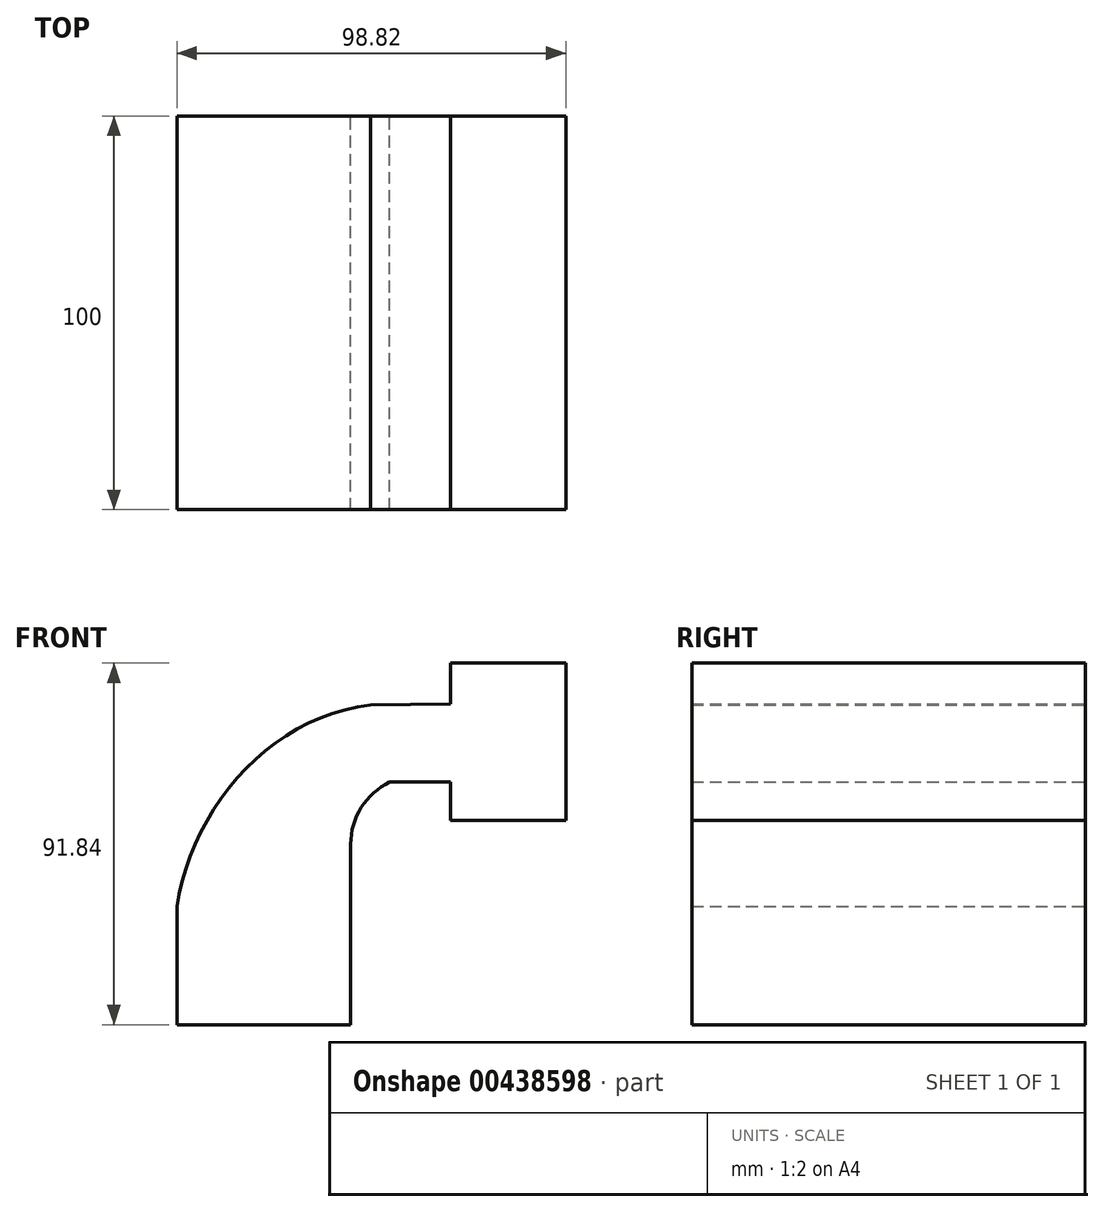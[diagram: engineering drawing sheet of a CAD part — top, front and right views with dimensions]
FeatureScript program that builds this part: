
annotation { "Feature Type Name" : "Feature", "Feature Type Description" : "" }
export const myFeature = defineFeature(function(context is Context, id is Id, definition is map)
    precondition{}
    {
        {
            var Q0;
            Q0=qCreatedBy(makeId("Front.planeOp"),FACE);
            var sketch = newSketch(context, id + "F0", { "sketchPlane" : qUnion([Q0])});
            skLineSegment(sketch, "E0.bottom", {"start": v(22.09, -15) * mm, "end": v(-22.09, -15) * mm});
            skLineSegment(sketch, "E0.top", {"start": v(22.09, 15) * mm, "end": v(-22.09, 15) * mm});
            skLineSegment(sketch, "E0.left", {"start": v(22.09, -15) * mm, "end": v(22.09, 15) * mm});
            skLineSegment(sketch, "E0.right", {"start": v(-22.09, -15) * mm, "end": v(-22.09, 15) * mm});
            skPoint(sketch, "E0.middle", {"position": v(0, 0) * mm});
            skLineSegment(sketch, "E1", {"start": v(22.09, 15) * mm, "end": v(22.09, 30.87) * mm});
            skArc(sketch, "E2", {"start": v(22.09, 30.87) * mm, "mid": v(24.77, 40.18) * mm, "end": v(32, 46.62) * mm});
            skLineSegment(sketch, "E3.bottom", {"start": v(76.73, 36.84) * mm, "end": v(47.44, 36.84) * mm});
            skLineSegment(sketch, "E3.top", {"start": v(76.73, 76.84) * mm, "end": v(47.44, 76.84) * mm});
            skLineSegment(sketch, "E3.left", {"start": v(76.73, 36.84) * mm, "end": v(76.73, 76.84) * mm});
            skLineSegment(sketch, "E3.right", {"start": v(47.44, 36.84) * mm, "end": v(47.44, 76.84) * mm});
            skPoint(sketch, "E3.middle", {"position": v(62.09, 56.84) * mm});
            skLineSegment(sketch, "E4.0", {"start": v(27.18, 66.24) * mm, "end": v(62.09, 66.62) * mm});
            skArc(sketch, "E4.1", {"start": v(2.09, 30.87) * mm, "mid": v(9, 52.55) * mm, "end": v(27.18, 66.24) * mm});
            skLineSegment(sketch, "E4.2", {"start": v(2.09, 15) * mm, "end": v(2.09, 30.87) * mm});
            skLineSegment(sketch, "E5", {"start": v(62.09, 56.84) * mm, "end": v(62.09, 76.84) * mm});
            skLineSegment(sketch, "E6", {"start": v(62.09, 76.84) * mm, "end": v(62.09, 56.84) * mm});
            skLineSegment(sketch, "E7", {"start": v(62.09, 56.84) * mm, "end": v(62.09, 36.84) * mm});
            skLineSegment(sketch, "E8", {"start": v(32, 46.62) * mm, "end": v(62.09, 46.62) * mm});
            skFitSpline(sketch, "E9", {"points": [v(-22.09, 15) * mm, v(27.18, 66.24) * mm], "startDerivative": vector(11.48, 74.86) * mm, "endDerivative": vector(77.05, 8.88) * mm});
            skSolve(sketch);
        }
        {
            var Q0;
            Q0 = qSketchRegion(id + "F0", true);
            extrude(context, id + "F1", {"entities" : qUnion([Q0]), "endBound" : BoundingType.SYMMETRIC, "depth" : 100 * mm});
        }
    });
